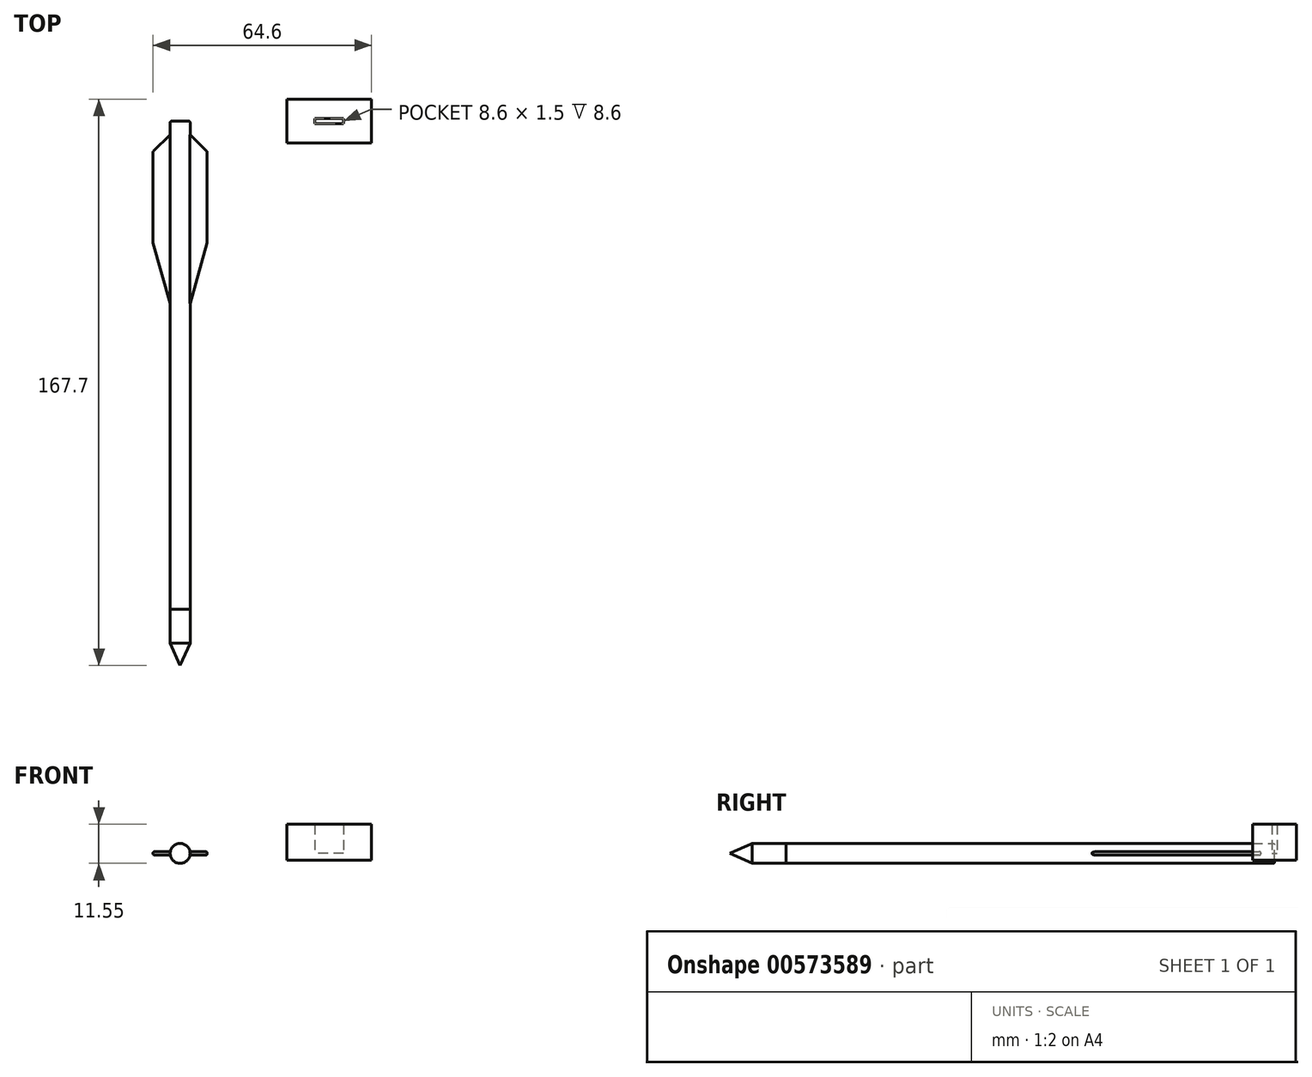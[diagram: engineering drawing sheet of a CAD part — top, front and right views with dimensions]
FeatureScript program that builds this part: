
annotation { "Feature Type Name" : "Feature", "Feature Type Description" : "" }
export const myFeature = defineFeature(function(context is Context, id is Id, definition is map)
    precondition{}
    {
        {
            var Q0;
            Q0=qCreatedBy(makeId("Front.planeOp"),FACE);
            var sketch = newSketch(context, id + "F0", { "sketchPlane" : qUnion([Q0])});
            skCircle(sketch, "E0", {"center": v(0, 0) * mm, "radius": 2.95 * mm});
            skLineSegment(sketch, "E1", {"start": v(-2.95, 0) * mm, "end": v(2.95, 0) * mm});
            skSolve(sketch);
        }
        {
            var Q0;
            {var subQ0=sQuery(id+"F0.wireOp",EDGE,"E1");Q0=makeQuery(id+"F0.imprint","IMPRINT",FACE,{"disambiguationData":[TD([[makeQuery(id+"F0.imprint","IMPRINT",EDGE,{"derivedFrom":subQ0}),-1.0]])]});}
            extrude(context, id + "F1", {"entities" : qUnion([Q0]), "depth" : 144.5 * mm, "offsetDistance" : 25 * mm});
        }
        {
            var Q0;
            Q0=qCreatedBy(makeId("Right.planeOp"),FACE);
            var sketch = newSketch(context, id + "F2", { "sketchPlane" : qUnion([Q0])});
            skLineSegment(sketch, "E2", {"start": v(0, 0) * mm, "end": v(-54, 0) * mm});
            skLineSegment(sketch, "E3", {"start": v(0, 0) * mm, "end": v(-4, 0) * mm});
            skLineSegment(sketch, "E4", {"start": v(-4, 0) * mm, "end": v(-4, 0.5) * mm});
            skLineSegment(sketch, "E5", {"start": v(-4, 0.5) * mm, "end": v(-54, 0.5) * mm});
            skLineSegment(sketch, "E6", {"start": v(-54, 0) * mm, "end": v(-54, 0.5) * mm});
            skLineSegment(sketch, "E7", {"start": v(-54, 0) * mm, "end": v(-54, -0.5) * mm});
            skLineSegment(sketch, "E8", {"start": v(-54, -0.5) * mm, "end": v(-4, -0.5) * mm});
            skLineSegment(sketch, "E9", {"start": v(-4, -0.5) * mm, "end": v(-4, 0) * mm});
            skSolve(sketch);
        }
        {
            var Q0;
            Q0=makeQuery(id+"F2.imprint","IMPRINT",FACE,{"disambiguationData":[TD([[makeQuery(id+"F2.imprint","IMPRINT",EDGE,{"derivedFrom":sQuery(id+"F2.wireOp",EDGE,"E2")}),-1.0]])]});
            extrude(context, id + "F3", {"entities" : qUnion([Q0]), "operationType" : NewBodyOperationType.ADD, "depth" : 8 * mm, "offsetDistance" : 25 * mm, "hasSecondDirection" : true, "secondDirectionOppositeDirection" : true, "secondDirectionDepth" : 8 * mm});
        }
        {
            var Q0;
            {var subQ0=sQuery(id+"F2.wireOp",EDGE,"E4");var subQ1=sQuery(id+"F2.wireOp",EDGE,"E6");var subQ2=sQuery(id+"F2.wireOp",EDGE,"E2");Q0=makeQuery(id+"F3.boolean.opBoolean","SPLIT",FACE,{"disambiguationData":[TD([makeQuery(id+"F3.opExtrude","CAP_FACE",FACE,{"disambiguationData":[OSD([subQ2,subQ0,sQuery(id+"F2.wireOp",EDGE,"E5"),subQ1])],"isStart":false})])],"derivedFrom":makeQuery(id+"F3.opExtrude","SWEPT_FACE",FACE,{"disambiguationData":[OSD([subQ2])]})});}
            var Q1;
            {var subQ0=sQuery(id+"F2.wireOp",EDGE,"E4");var subQ1=sQuery(id+"F2.wireOp",EDGE,"E6");var subQ2=sQuery(id+"F2.wireOp",EDGE,"E2");Q1=makeQuery(id+"F3.boolean.opBoolean","SPLIT",FACE,{"disambiguationData":[TD([makeQuery(id+"F3.opExtrude","CAP_FACE",FACE,{"disambiguationData":[OSD([subQ2,subQ0,sQuery(id+"F2.wireOp",EDGE,"E5"),subQ1])],"isStart":true})])],"derivedFrom":makeQuery(id+"F3.opExtrude","SWEPT_FACE",FACE,{"disambiguationData":[OSD([subQ2])]})});}
            extrude(context, id + "F4", {"entities" : qUnion([Q0, Q1]), "operationType" : NewBodyOperationType.ADD, "depth" : .5 * mm, "offsetDistance" : 25 * mm});
        }
        {
            var Q0;
            {var subQ0=sQuery(id+"F0.wireOp",EDGE,"E0");var subQ1=sQuery(id+"F0.wireOp",EDGE,"E1");Q0=makeQuery(id+"F4.opExtrude","SWEPT_FACE",FACE,{"disambiguationData":[OSD([subQ0,subQ1]),TDD([makeQuery(id+"F3.boolean.opBoolean","SPLIT",EDGE,{"disambiguationData":[topologyDisambiguationEdgeConnected([makeQuery(id+"F1.opExtrude","SWEPT_FACE",FACE,{"disambiguationData":[OSD([subQ0])]}),makeQuery(id+"F3.opExtrude","SWEPT_FACE",FACE,{"disambiguationData":[OSD([sQuery(id+"F2.wireOp",EDGE,"E2")])]})])],"derivedFrom":makeQuery(id+"F1.opExtrude","SWEPT_EDGE",EDGE,{"disambiguationData":[OSD([subQ0,subQ1]),TDD([makeQuery(id+"F0.imprint","INTERSECT",VERTEX,{"disambiguationData":[OD(1.0)],"derivedFrom":[subQ0,subQ1]})])]})})])]});}
            extrude(context, id + "F5", {"entities" : qUnion([Q0]), "operationType" : NewBodyOperationType.ADD, "depth" : 6 * mm, "offsetDistance" : 25 * mm});
        }
        {
            var Q0;
            Q0=makeQuery(id+"F3.opExtrude","SWEPT_FACE",FACE,{"disambiguationData":[OSD([sQuery(id+"F2.wireOp",EDGE,"E5")])]});
            extrude(context, id + "F6", {"entities" : qUnion([Q0]), "operationType" : NewBodyOperationType.REMOVE, "oppositeDirection" : true, "depth" : .5 * mm, "offsetDistance" : 25 * mm});
        }
        {
            var Q0;
            {var subQ2=sQuery(id+"F0.wireOp",EDGE,"E1");var subQ4=makeQuery(id+"F1.opExtrude","SWEPT_FACE",FACE,{"disambiguationData":[OSD([subQ2])]});Q0=makeQuery(id+"F6.boolean.opBoolean","MERGE",FACE,{"derivedFrom":[makeQuery(id+"F3.boolean.opBoolean","SPLIT",FACE,{"disambiguationData":[TD([makeQuery(id+"F3.opExtrude","SWEPT_FACE",FACE,{"disambiguationData":[OSD([sQuery(id+"F2.wireOp",EDGE,"E4")])]})])],"derivedFrom":subQ4}),makeQuery(id+"F3.boolean.opBoolean","SPLIT",FACE,{"disambiguationData":[TD([makeQuery(id+"F3.opExtrude","SWEPT_FACE",FACE,{"disambiguationData":[OSD([sQuery(id+"F2.wireOp",EDGE,"E6")])]})])],"derivedFrom":subQ4}),makeQuery(id+"F6.opExtrude","CAP_FACE",FACE,{"disambiguationData":[OSD([sQuery(id+"F2.wireOp",EDGE,"E5")])],"isStart":false})]});}
            var sketch = newSketch(context, id + "F7", { "sketchPlane" : qUnion([Q0])});
            skLineSegment(sketch, "E10", {"start": v(2.95, -4) * mm, "end": v(-2.95, -4) * mm});
            skLineSegment(sketch, "E11", {"start": v(-2.95, -4) * mm, "end": v(-2.95, -9) * mm});
            skLineSegment(sketch, "E12", {"start": v(-2.95, -9) * mm, "end": v(2.95, -9) * mm});
            skLineSegment(sketch, "E13", {"start": v(2.95, -9) * mm, "end": v(2.95, -4) * mm});
            skLineSegment(sketch, "E14", {"start": v(-2.95, -9) * mm, "end": v(-8, -9) * mm});
            skLineSegment(sketch, "E15", {"start": v(-8, -9) * mm, "end": v(8, -9) * mm});
            skLineSegment(sketch, "E16", {"start": v(-2.95, -4) * mm, "end": v(-8, -9) * mm});
            skLineSegment(sketch, "E17", {"start": v(8, -9) * mm, "end": v(2.95, -4) * mm});
            skLineSegment(sketch, "E18", {"start": v(2.95, -54) * mm, "end": v(2.95, -36) * mm});
            skLineSegment(sketch, "E19", {"start": v(2.95, -36) * mm, "end": v(-2.95, -36) * mm});
            skLineSegment(sketch, "E20", {"start": v(-2.95, -36) * mm, "end": v(-2.95, -54) * mm});
            skLineSegment(sketch, "E21", {"start": v(2.95, -54) * mm, "end": v(8, -36) * mm});
            skLineSegment(sketch, "E22", {"start": v(8, -36) * mm, "end": v(-8, -36) * mm});
            skLineSegment(sketch, "E23", {"start": v(-8, -36) * mm, "end": v(-2.95, -54) * mm});
            skLineSegment(sketch, "E24", {"start": v(-2.95, -54) * mm, "end": v(2.95, -54) * mm});
            skLineSegment(sketch, "E25", {"start": v(-2.95, -4) * mm, "end": v(2.95, -4) * mm});
            skSolve(sketch);
        }
        {
            var Q0;
            {var subQ0=sQuery(id+"F7.wireOp",EDGE,"E16");Q0=makeQuery(id+"F7.imprint","IMPRINT",FACE,{"disambiguationData":[TD([[makeQuery(id+"F7.imprint","IMPRINT",EDGE,{"derivedFrom":subQ0}),-1.0]])]});}
            var Q1;
            {var subQ0=sQuery(id+"F7.wireOp",EDGE,"E23");Q1=makeQuery(id+"F7.imprint","IMPRINT",FACE,{"disambiguationData":[TD([[makeQuery(id+"F7.imprint","IMPRINT",EDGE,{"derivedFrom":subQ0}),-1.0]])]});}
            var Q2;
            {var subQ0=sQuery(id+"F7.wireOp",EDGE,"E21");Q2=makeQuery(id+"F7.imprint","IMPRINT",FACE,{"disambiguationData":[TD([[makeQuery(id+"F7.imprint","IMPRINT",EDGE,{"derivedFrom":subQ0}),-1.0]])]});}
            var Q3;
            {var subQ0=sQuery(id+"F7.wireOp",EDGE,"E17");Q3=makeQuery(id+"F7.imprint","IMPRINT",FACE,{"disambiguationData":[TD([[makeQuery(id+"F7.imprint","IMPRINT",EDGE,{"derivedFrom":subQ0}),-1.0]])]});}
            extrude(context, id + "F8", {"entities" : qUnion([Q0, Q1, Q2, Q3]), "operationType" : NewBodyOperationType.REMOVE, "oppositeDirection" : true, "depth" : .5 * mm, "offsetDistance" : 25 * mm});
        }
        {
            var Q0;
            {var subQ0=sQuery(id+"F7.wireOp",EDGE,"E11");Q0=makeQuery(id+"F7.imprint","IMPRINT",FACE,{"disambiguationData":[TD([[makeQuery(id+"F7.imprint","IMPRINT",EDGE,{"derivedFrom":subQ0}),1.0]])]});}
            var Q1;
            {var subQ5=sQuery(id+"F7.wireOp",EDGE,"E15");var subQ8=makeQuery(id+"F7.imprint","INTERSECT",VERTEX,{"derivedFrom":[sQuery(id+"F7.wireOp",EDGE,"E11"),subQ5]});Q1=makeQuery(id+"F7.imprint","IMPRINT",FACE,{"disambiguationData":[TD([[makeQuery(id+"F7.imprint","IMPRINT",EDGE,{"disambiguationData":[TD([[subQ8,-1.0]])],"derivedFrom":subQ5}),-1.0]])]});}
            var Q2;
            {var subQ0=sQuery(id+"F7.wireOp",EDGE,"E11");Q2=makeQuery(id+"F7.imprint","IMPRINT",FACE,{"disambiguationData":[TD([[makeQuery(id+"F7.imprint","IMPRINT",EDGE,{"derivedFrom":subQ0}),-1.0]])]});}
            var Q3;
            {var subQ0=sQuery(id+"F7.wireOp",EDGE,"E13");Q3=makeQuery(id+"F7.imprint","IMPRINT",FACE,{"disambiguationData":[TD([[makeQuery(id+"F7.imprint","IMPRINT",EDGE,{"derivedFrom":subQ0}),-1.0]])]});}
            var Q4;
            {var subQ0=sQuery(id+"F7.wireOp",EDGE,"E18");Q4=makeQuery(id+"F7.imprint","IMPRINT",FACE,{"disambiguationData":[TD([[makeQuery(id+"F7.imprint","IMPRINT",EDGE,{"derivedFrom":subQ0}),-1.0]])]});}
            var Q5;
            {var subQ0=sQuery(id+"F7.wireOp",EDGE,"E20");Q5=makeQuery(id+"F7.imprint","IMPRINT",FACE,{"disambiguationData":[TD([[makeQuery(id+"F7.imprint","IMPRINT",EDGE,{"derivedFrom":subQ0}),-1.0]])]});}
            var Q6;
            {var subQ0=sQuery(id+"F7.wireOp",EDGE,"E18");Q6=makeQuery(id+"F7.imprint","IMPRINT",FACE,{"disambiguationData":[TD([[makeQuery(id+"F7.imprint","IMPRINT",EDGE,{"derivedFrom":subQ0}),1.0]])]});}
            extrude(context, id + "F9", {"entities" : qUnion([Q0, Q1, Q2, Q3, Q4, Q5, Q6]), "operationType" : NewBodyOperationType.ADD, "depth" : .5 * mm, "offsetDistance" : 25 * mm});
        }
        {
            var Q0;
            {var subQ0=sQuery(id+"F0.wireOp",EDGE,"E1");Q0=makeQuery(id+"F0.imprint","IMPRINT",FACE,{"disambiguationData":[TD([[makeQuery(id+"F0.imprint","IMPRINT",EDGE,{"derivedFrom":subQ0}),1.0]])]});}
            extrude(context, id + "F10", {"entities" : qUnion([Q0]), "operationType" : NewBodyOperationType.ADD, "depth" : 144.5 * mm, "offsetDistance" : 25 * mm});
        }
        {
            var Q0;
            {var subQ0=sQuery(id+"F7.wireOp",EDGE,"E23");Q0=makeQuery(id+"F9.boolean.opBoolean","MERGE",FACE,{"derivedFrom":[makeQuery(id+"F8.boolean.opBoolean","COPY",FACE,{"derivedFrom":makeQuery(id+"F8.opExtrude","SWEPT_FACE",FACE,{"disambiguationData":[OSD([subQ0])]})}),makeQuery(id+"F9.opExtrude","SWEPT_FACE",FACE,{"disambiguationData":[OSD([subQ0])]})]});}
            var Q1;
            {var subQ0=sQuery(id+"F7.wireOp",EDGE,"E21");Q1=makeQuery(id+"F9.boolean.opBoolean","MERGE",FACE,{"derivedFrom":[makeQuery(id+"F8.boolean.opBoolean","COPY",FACE,{"derivedFrom":makeQuery(id+"F8.opExtrude","SWEPT_FACE",FACE,{"disambiguationData":[OSD([subQ0])]})}),makeQuery(id+"F9.opExtrude","SWEPT_FACE",FACE,{"disambiguationData":[OSD([subQ0])]})]});}
            var Q2;
            {var subQ0=sQuery(id+"F2.wireOp",EDGE,"E5");var subQ1=makeQuery(id+"F6.boolean.opBoolean","COPY",EDGE,{"derivedFrom":makeQuery(id+"F6.opExtrude","CAP_EDGE",EDGE,{"disambiguationData":[OSD([subQ0]),TDD([makeQuery(id+"F3.opExtrude","CAP_EDGE",EDGE,{"disambiguationData":[OSD([subQ0])],"isStart":false})])],"isStart":false})});var subQ2=sQuery(id+"F2.wireOp",EDGE,"E2");Q2=makeQuery(id+"F9.boolean.opBoolean","MERGE",FACE,{"derivedFrom":[makeQuery(id+"F4.boolean.opBoolean","MERGE",FACE,{"derivedFrom":[makeQuery(id+"F3.opExtrude","CAP_FACE",FACE,{"disambiguationData":[OSD([subQ2,sQuery(id+"F2.wireOp",EDGE,"E4"),subQ0,sQuery(id+"F2.wireOp",EDGE,"E6")])],"isStart":false}),makeQuery(id+"F4.opExtrude","SWEPT_FACE",FACE,{"disambiguationData":[OSD([subQ2]),TDD([makeQuery(id+"F3.opExtrude","CAP_EDGE",EDGE,{"disambiguationData":[OSD([subQ2])],"isStart":false})])]})]}),makeQuery(id+"F9.opExtrude","SWEPT_FACE",FACE,{"disambiguationData":[OSD([subQ0]),TDD([makeQuery(id+"F7.imprint","IMPRINT",EDGE,{"disambiguationData":[TD([[makeQuery(id+"F7.imprint","INTERSECT",VERTEX,{"derivedFrom":[subQ1,sQuery(id+"F7.wireOp",EDGE,"E15"),sQuery(id+"F7.wireOp",EDGE,"E17")]}),-1.0]])],"derivedFrom":subQ1})])]})]});}
            var Q3;
            {var subQ0=sQuery(id+"F7.wireOp",EDGE,"E17");Q3=makeQuery(id+"F9.boolean.opBoolean","MERGE",FACE,{"derivedFrom":[makeQuery(id+"F8.boolean.opBoolean","COPY",FACE,{"derivedFrom":makeQuery(id+"F8.opExtrude","SWEPT_FACE",FACE,{"disambiguationData":[OSD([subQ0])]})}),makeQuery(id+"F9.opExtrude","SWEPT_FACE",FACE,{"disambiguationData":[OSD([subQ0])]})]});}
            var Q4;
            {var subQ0=sQuery(id+"F2.wireOp",EDGE,"E5");var subQ1=makeQuery(id+"F6.boolean.opBoolean","COPY",EDGE,{"derivedFrom":makeQuery(id+"F6.opExtrude","CAP_EDGE",EDGE,{"disambiguationData":[OSD([subQ0]),TDD([makeQuery(id+"F3.opExtrude","CAP_EDGE",EDGE,{"disambiguationData":[OSD([subQ0])],"isStart":true})])],"isStart":false})});var subQ2=sQuery(id+"F2.wireOp",EDGE,"E2");Q4=makeQuery(id+"F9.boolean.opBoolean","MERGE",FACE,{"derivedFrom":[makeQuery(id+"F4.boolean.opBoolean","MERGE",FACE,{"derivedFrom":[makeQuery(id+"F3.opExtrude","CAP_FACE",FACE,{"disambiguationData":[OSD([subQ2,sQuery(id+"F2.wireOp",EDGE,"E4"),subQ0,sQuery(id+"F2.wireOp",EDGE,"E6")])],"isStart":true}),makeQuery(id+"F4.opExtrude","SWEPT_FACE",FACE,{"disambiguationData":[OSD([subQ2]),TDD([makeQuery(id+"F3.opExtrude","CAP_EDGE",EDGE,{"disambiguationData":[OSD([subQ2])],"isStart":true})])]})]}),makeQuery(id+"F9.opExtrude","SWEPT_FACE",FACE,{"disambiguationData":[OSD([subQ0]),TDD([makeQuery(id+"F7.imprint","IMPRINT",EDGE,{"disambiguationData":[TD([[makeQuery(id+"F7.imprint","INTERSECT",VERTEX,{"derivedFrom":[subQ1,sQuery(id+"F7.wireOp",EDGE,"E15"),sQuery(id+"F7.wireOp",EDGE,"E16")]}),-1.0]])],"derivedFrom":subQ1})])]})]});}
            var Q5;
            {var subQ0=sQuery(id+"F7.wireOp",EDGE,"E16");Q5=makeQuery(id+"F9.boolean.opBoolean","MERGE",FACE,{"derivedFrom":[makeQuery(id+"F8.boolean.opBoolean","COPY",FACE,{"derivedFrom":makeQuery(id+"F8.opExtrude","SWEPT_FACE",FACE,{"disambiguationData":[OSD([subQ0])]})}),makeQuery(id+"F9.opExtrude","SWEPT_FACE",FACE,{"disambiguationData":[OSD([subQ0])]})]});}
            var Q6;
            {var subQ0=sQuery(id+"F0.wireOp",EDGE,"E1");var subQ1=sQuery(id+"F0.wireOp",EDGE,"E0");Q6=makeQuery(id+"F10.boolean.opBoolean","MERGE",FACE,{"derivedFrom":[makeQuery(id+"F1.opExtrude","CAP_FACE",FACE,{"disambiguationData":[OSD([subQ1,subQ0])],"isStart":true}),makeQuery(id+"F10.opExtrude","CAP_FACE",FACE,{"disambiguationData":[OSD([subQ1,subQ0])],"isStart":true})]});}
            fillet(context, id + "F11", {"entities" : qUnion([Q0, Q1, Q2, Q3, Q4, Q5, Q6]), "radius" : .4 * mm, "tangentPropagation" : true, "allowEdgeOverflow" : false});
        }
        {
            var Q0;
            Q0=qCreatedBy(makeId("Right.planeOp"),FACE);
            var sketch = newSketch(context, id + "F12", { "sketchPlane" : qUnion([Q0])});
            skLineSegment(sketch, "E26", {"start": v(0, 0) * mm, "end": v(-144.5, 0) * mm});
            skLineSegment(sketch, "E27", {"start": v(-144.5, 0) * mm, "end": v(-144.5, 2.95) * mm});
            skLineSegment(sketch, "E28", {"start": v(-144.5, 0) * mm, "end": v(-161.2, 0) * mm});
            skLineSegment(sketch, "E29", {"start": v(-144.5, 2.95) * mm, "end": v(-154.5, 2.95) * mm});
            skLineSegment(sketch, "E30", {"start": v(-154.5, 2.95) * mm, "end": v(-161.2, 0) * mm});
            skSolve(sketch);
        }
        {
            var Q0;
            Q0=makeQuery(id+"F12.imprint","IMPRINT",FACE,{"disambiguationData":[TD([[makeQuery(id+"F12.imprint","IMPRINT",EDGE,{"derivedFrom":sQuery(id+"F12.wireOp",EDGE,"E27")}),1.0]])]});
            var Q1;
            Q1=sQuery(id+"F12.wireOp",EDGE,"E28");
            revolve(context, id + "F13", {"entities" : qUnion([Q0]), "axis" : qUnion([Q1]), "revolveType" : RevolveType.FULL});
        }
        {
            var Q0;
            Q0=qCreatedBy(makeId("Top.planeOp"),FACE);
            var sketch = newSketch(context, id + "F14", { "sketchPlane" : qUnion([Q0])});
            skLineSegment(sketch, "E31.bottom", {"start": v(48.4, -0.75) * mm, "end": v(39.8, -0.75) * mm});
            skLineSegment(sketch, "E31.top", {"start": v(48.4, 0.75) * mm, "end": v(39.8, 0.75) * mm});
            skLineSegment(sketch, "E31.left", {"start": v(48.4, -0.75) * mm, "end": v(48.4, 0.75) * mm});
            skLineSegment(sketch, "E31.right", {"start": v(39.8, -0.75) * mm, "end": v(39.8, 0.75) * mm});
            skPoint(sketch, "E31.middle", {"position": v(44.1, 0) * mm});
            skLineSegment(sketch, "E32.bottom", {"start": v(56.6, -6.5) * mm, "end": v(31.6, -6.5) * mm});
            skLineSegment(sketch, "E32.top", {"start": v(56.6, 6.5) * mm, "end": v(31.6, 6.5) * mm});
            skLineSegment(sketch, "E32.left", {"start": v(56.6, -6.5) * mm, "end": v(56.6, 6.5) * mm});
            skLineSegment(sketch, "E32.right", {"start": v(31.6, -6.5) * mm, "end": v(31.6, 6.5) * mm});
            skSolve(sketch);
        }
        {
            var Q0;
            Q0=makeQuery(id+"F14.imprint","IMPRINT",FACE,{"disambiguationData":[TD([[makeQuery(id+"F14.imprint","IMPRINT",EDGE,{"derivedFrom":sQuery(id+"F14.wireOp",EDGE,"E31.bottom")}),1.0]])]});
            extrude(context, id + "F15", {"entities" : qUnion([Q0]), "depth" : 8.6 * mm, "offsetDistance" : 25 * mm});
        }
        {
            var Q0;
            Q0=makeQuery(id+"F14.imprint","IMPRINT",FACE,{"disambiguationData":[TD([[makeQuery(id+"F14.imprint","IMPRINT",EDGE,{"derivedFrom":sQuery(id+"F14.wireOp",EDGE,"E31.bottom")}),-1.0]])]});
            var Q1;
            Q1=makeQuery(id+"F14.imprint","IMPRINT",FACE,{"disambiguationData":[TD([[makeQuery(id+"F14.imprint","IMPRINT",EDGE,{"derivedFrom":sQuery(id+"F14.wireOp",EDGE,"E31.bottom")}),1.0]])]});
            extrude(context, id + "F16", {"entities" : qUnion([Q0, Q1]), "operationType" : NewBodyOperationType.ADD, "oppositeDirection" : true, "depth" : 2 * mm, "offsetDistance" : 25 * mm});
        }
    });
